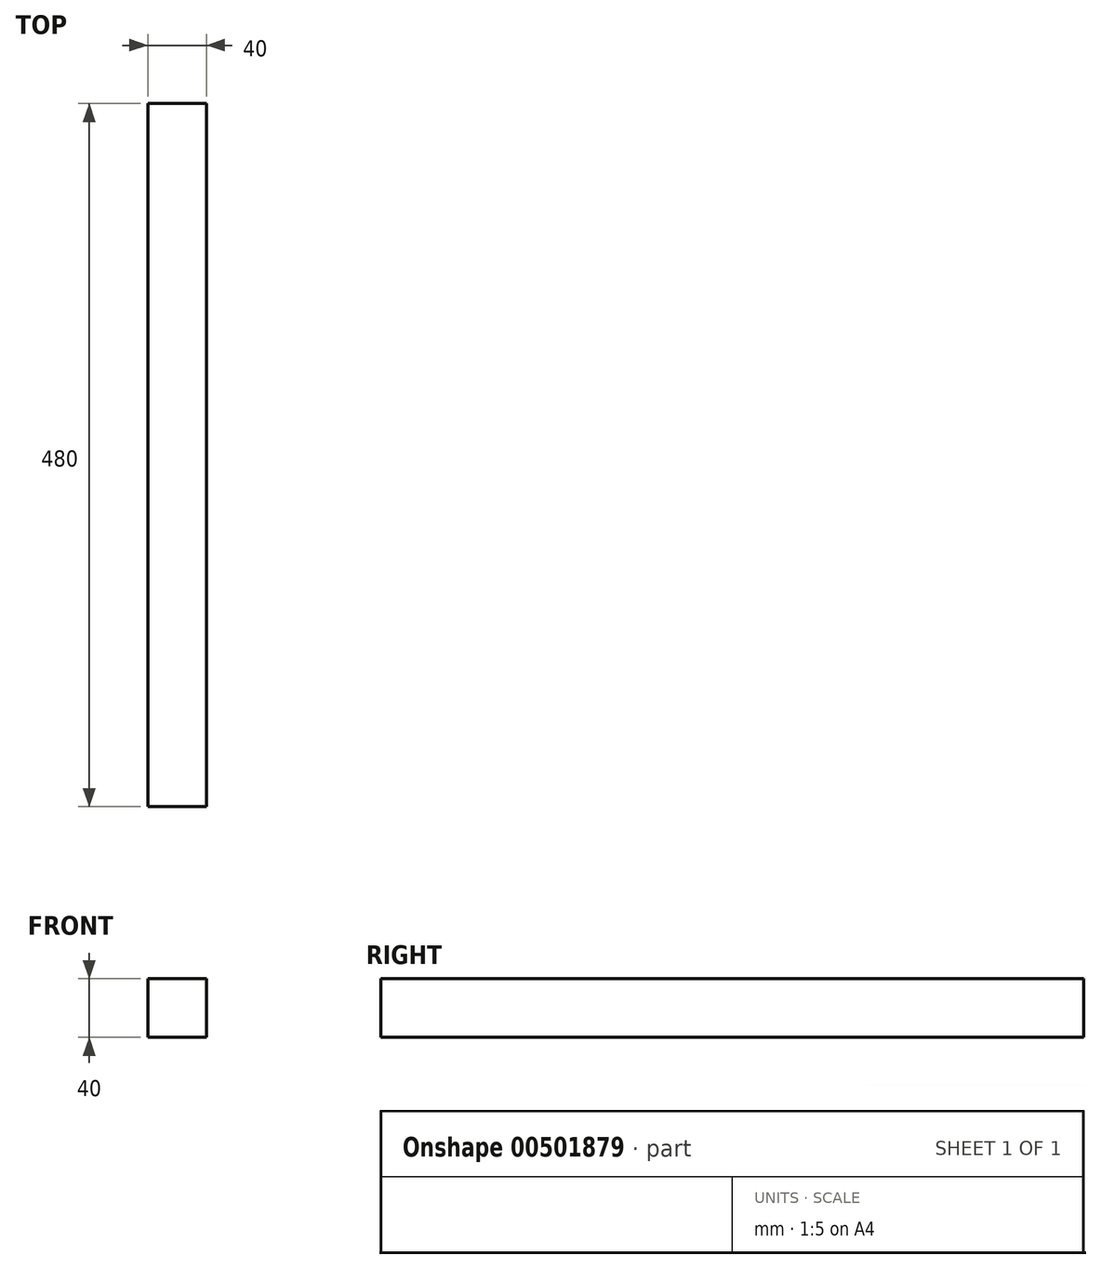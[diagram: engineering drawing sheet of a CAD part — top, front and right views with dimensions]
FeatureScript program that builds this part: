
annotation { "Feature Type Name" : "Feature", "Feature Type Description" : "" }
export const myFeature = defineFeature(function(context is Context, id is Id, definition is map)
    precondition{}
    {
        {
            var Q0;
            Q0=qCreatedBy(makeId("Front.planeOp"),FACE);
            var sketch = newSketch(context, id + "F0", { "sketchPlane" : qUnion([Q0])});
            skLineSegment(sketch, "E0.bottom", {"start": v(-20, 20) * mm, "end": v(20, 20) * mm});
            skLineSegment(sketch, "E0.top", {"start": v(-20, -20) * mm, "end": v(20, -20) * mm});
            skLineSegment(sketch, "E0.left", {"start": v(-20, 20) * mm, "end": v(-20, -20) * mm});
            skLineSegment(sketch, "E0.right", {"start": v(20, 20) * mm, "end": v(20, -20) * mm});
            skSolve(sketch);
        }
        {
            var Q0;
            Q0=makeQuery(id+"F0.imprint","IMPRINT",FACE,{"disambiguationData":[TD([[makeQuery(id+"F0.imprint","IMPRINT",EDGE,{"derivedFrom":sQuery(id+"F0.wireOp",EDGE,"E0.bottom")}),-1.0]])]});
            extrude(context, id + "F1", {"entities" : qUnion([Q0]), "depth" : 480 * mm});
        }
    });
